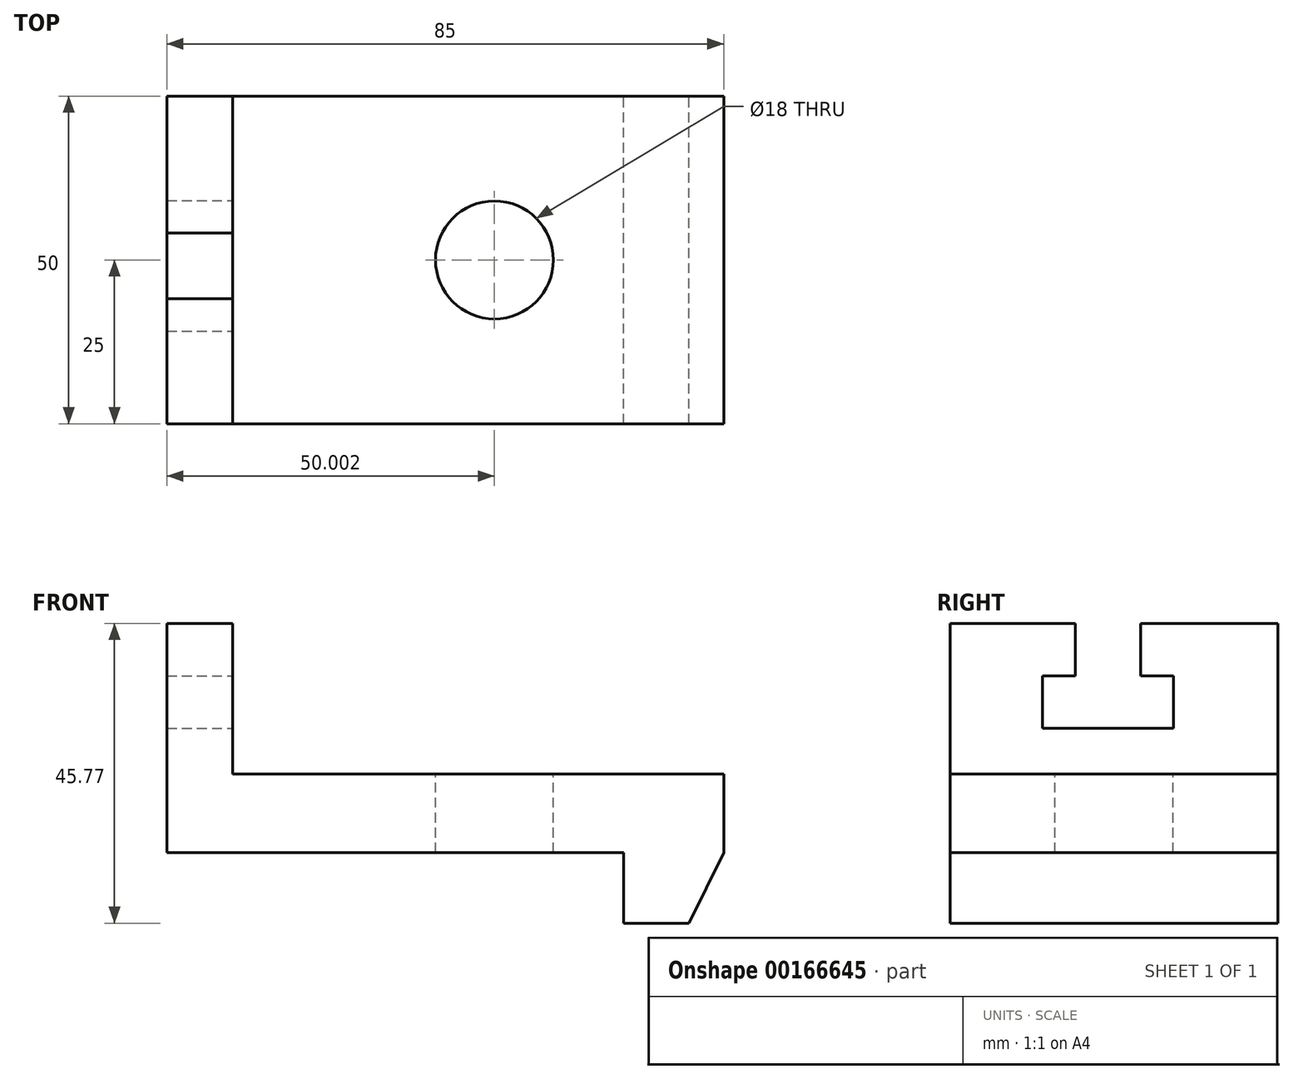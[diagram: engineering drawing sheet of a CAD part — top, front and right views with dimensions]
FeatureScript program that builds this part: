
annotation { "Feature Type Name" : "Feature", "Feature Type Description" : "" }
export const myFeature = defineFeature(function(context is Context, id is Id, definition is map)
    precondition{}
    {
        {
            var Q0;
            Q0=qCreatedBy(makeId("Front.planeOp"),FACE);
            var sketch = newSketch(context, id + "F0", { "sketchPlane" : qUnion([Q0])});
            skLineSegment(sketch, "E0", {"start": v(-26.02, 6) * mm, "end": v(48.98, 6) * mm});
            skLineSegment(sketch, "E1", {"start": v(-36.02, -6) * mm, "end": v(33.69, -6) * mm});
            skLineSegment(sketch, "E2", {"start": v(48.98, 6) * mm, "end": v(48.98, -6) * mm});
            skPoint(sketch, "E3.start.orphan", {"position": v(-36.02, 0) * mm});
            skLineSegment(sketch, "E4", {"start": v(-36.02, -6) * mm, "end": v(-36.02, 29) * mm});
            skLineSegment(sketch, "E5", {"start": v(-36.02, 29) * mm, "end": v(-26.02, 29) * mm});
            skLineSegment(sketch, "E6", {"start": v(-26.02, 29) * mm, "end": v(-26.02, 6) * mm});
            skLineSegment(sketch, "E7", {"start": v(48.98, -6) * mm, "end": v(43.69, -16.77) * mm});
            skPoint(sketch, "E8.end.orphan", {"position": v(48.98, -20.01) * mm});
            skLineSegment(sketch, "E9", {"start": v(43.69, -16.77) * mm, "end": v(33.69, -16.77) * mm});
            skLineSegment(sketch, "E10", {"start": v(33.69, -16.77) * mm, "end": v(33.69, -6) * mm});
            skSolve(sketch);
        }
        {
            var Q0;
            Q0 = qSketchRegion(id + "F0", true);
            extrude(context, id + "F1", {"entities" : qUnion([Q0]), "depth" : 50 * mm});
        }
        {
            var Q0;
            Q0=makeQuery(id+"F1.opExtrude","SWEPT_FACE",FACE,{"disambiguationData":[OSD([sQuery(id+"F0.wireOp",EDGE,"E6")])]});
            var sketch = newSketch(context, id + "F2", { "sketchPlane" : qUnion([Q0])});
            skLineSegment(sketch, "E11", {"start": v(-30.9, 29) * mm, "end": v(-20.9, 29) * mm});
            skLineSegment(sketch, "E12", {"start": v(-20.9, 29) * mm, "end": v(-20.9, 21) * mm});
            skLineSegment(sketch, "E13", {"start": v(-30.9, 29) * mm, "end": v(-30.9, 21) * mm});
            skLineSegment(sketch, "E14", {"start": v(-30.9, 21) * mm, "end": v(-35.9, 21) * mm});
            skLineSegment(sketch, "E15", {"start": v(-20.9, 21) * mm, "end": v(-15.9, 21) * mm});
            skLineSegment(sketch, "E16", {"start": v(-35.9, 21) * mm, "end": v(-35.9, 13) * mm});
            skLineSegment(sketch, "E17", {"start": v(-15.9, 21) * mm, "end": v(-15.9, 13) * mm});
            skLineSegment(sketch, "E18", {"start": v(-35.9, 13) * mm, "end": v(-15.9, 13) * mm});
            skSolve(sketch);
        }
        {
            var Q0;
            Q0 = qSketchRegion(id + "F2", true);
            extrude(context, id + "F3", {"entities" : qUnion([Q0]), "operationType" : NewBodyOperationType.REMOVE, "oppositeDirection" : true, "depth" : 25 * mm});
        }
        {
            var Q0;
            Q0=makeQuery(id+"F1.opExtrude","SWEPT_FACE",FACE,{"disambiguationData":[OSD([sQuery(id+"F0.wireOp",EDGE,"E0")])]});
            var sketch = newSketch(context, id + "F4", { "sketchPlane" : qUnion([Q0])});
            skCircle(sketch, "E19", {"center": v(13.98, -25) * mm, "radius": 9 * mm});
            skSolve(sketch);
        }
        {
            var Q0;
            Q0 = qSketchRegion(id + "F4", true);
            extrude(context, id + "F5", {"entities" : qUnion([Q0]), "operationType" : NewBodyOperationType.REMOVE, "oppositeDirection" : true, "depth" : 25 * mm});
        }
    });
